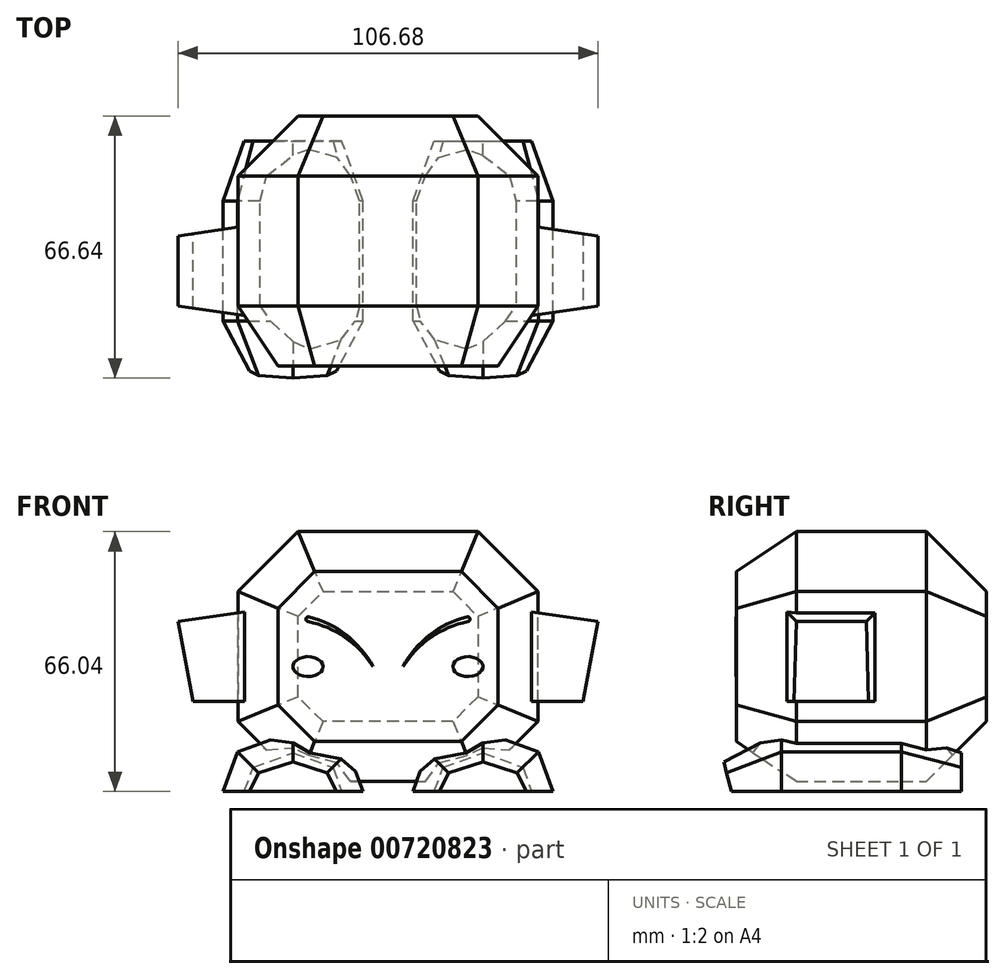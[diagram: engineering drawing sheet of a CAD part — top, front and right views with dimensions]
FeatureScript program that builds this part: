
annotation { "Feature Type Name" : "Feature", "Feature Type Description" : "" }
export const myFeature = defineFeature(function(context is Context, id is Id, definition is map)
    precondition{}
    {
        {
            var Q0;
            Q0=qCreatedBy(makeId("Front.planeOp"),FACE);
            var sketch = newSketch(context, id + "F0", { "sketchPlane" : qUnion([Q0])});
            skLineSegment(sketch, "E0.bottom", {"start": v(38.1, 31.75) * mm, "end": v(-38.1, 31.75) * mm});
            skLineSegment(sketch, "E0.top", {"start": v(38.1, -31.75) * mm, "end": v(-38.1, -31.75) * mm});
            skLineSegment(sketch, "E0.left", {"start": v(38.1, 31.75) * mm, "end": v(38.1, -31.75) * mm});
            skLineSegment(sketch, "E0.right", {"start": v(-38.1, 31.75) * mm, "end": v(-38.1, -31.75) * mm});
            skPoint(sketch, "E0.middle", {"position": v(0, 0) * mm});
            skSolve(sketch);
        }
        {
            var Q0;
            Q0=makeQuery(id+"F0.imprint","IMPRINT",FACE,{"disambiguationData":[TD([[makeQuery(id+"F0.imprint","IMPRINT",EDGE,{"derivedFrom":sQuery(id+"F0.wireOp",EDGE,"E0.bottom")}),1.0]])]});
            extrude(context, id + "F1", {"entities" : qUnion([Q0]), "depth" : 63.5 * mm, "offsetDistance" : 25.4 * mm, "symmetric" : true});
        }
        {
            var Q0;
            Q0=makeQuery(id+"F1.opExtrude","SWEPT_EDGE",EDGE,{"disambiguationData":[OSD([sQuery(id+"F0.wireOp",EDGE,"E0.bottom"),sQuery(id+"F0.wireOp",EDGE,"E0.right")])]});
            var Q1;
            Q1=makeQuery(id+"F1.opExtrude","SWEPT_EDGE",EDGE,{"disambiguationData":[OSD([sQuery(id+"F0.wireOp",EDGE,"E0.bottom"),sQuery(id+"F0.wireOp",EDGE,"E0.left")])]});
            var Q2;
            Q2=makeQuery(id+"F1.opExtrude","SWEPT_EDGE",EDGE,{"disambiguationData":[OSD([sQuery(id+"F0.wireOp",EDGE,"E0.top"),sQuery(id+"F0.wireOp",EDGE,"E0.right")])]});
            var Q3;
            Q3=makeQuery(id+"F1.opExtrude","SWEPT_EDGE",EDGE,{"disambiguationData":[OSD([sQuery(id+"F0.wireOp",EDGE,"E0.top"),sQuery(id+"F0.wireOp",EDGE,"E0.left")])]});
            chamfer(context, id + "F2", {"entities" : qUnion([Q0, Q1, Q2, Q3]), "width" : 15.24 * mm, "tangentPropagation" : true});
        }
        {
            var Q0;
            Q0=makeQuery(id+"F1.opExtrude","CAP_FACE",FACE,{"disambiguationData":[OSD([sQuery(id+"F0.wireOp",EDGE,"E0.bottom"),sQuery(id+"F0.wireOp",EDGE,"E0.top"),sQuery(id+"F0.wireOp",EDGE,"E0.left"),sQuery(id+"F0.wireOp",EDGE,"E0.right")])],"isStart":false});
            chamfer(context, id + "F3", {"entities" : qUnion([Q0]), "chamferType" : ChamferType.TWO_OFFSETS, "width1" : 10.16 * mm, "oppositeDirection" : false, "width2" : 15.24 * mm, "tangentPropagation" : true});
        }
        {
            var Q0;
            Q0=makeQuery(id+"F1.opExtrude","CAP_FACE",FACE,{"disambiguationData":[OSD([sQuery(id+"F0.wireOp",EDGE,"E0.bottom"),sQuery(id+"F0.wireOp",EDGE,"E0.top"),sQuery(id+"F0.wireOp",EDGE,"E0.left"),sQuery(id+"F0.wireOp",EDGE,"E0.right")])],"isStart":true});
            chamfer(context, id + "F4", {"entities" : qUnion([Q0]), "chamferType" : ChamferType.TWO_OFFSETS, "width1" : 15.24 * mm, "oppositeDirection" : false, "width2" : 15.24 * mm, "tangentPropagation" : true});
        }
        {
            var Q0;
            Q0=qCreatedBy(makeId("Right.planeOp"),FACE);
            var sketch = newSketch(context, id + "F5", { "sketchPlane" : qUnion([Q0])});
            skLineSegment(sketch, "E1.bottom", {"start": v(-19.05, 11.43) * mm, "end": v(3.81, 11.43) * mm});
            skLineSegment(sketch, "E1.top", {"start": v(-19.05, -11.43) * mm, "end": v(3.81, -11.43) * mm});
            skLineSegment(sketch, "E1.left", {"start": v(-19.05, 11.43) * mm, "end": v(-19.05, -11.43) * mm});
            skLineSegment(sketch, "E1.right", {"start": v(3.81, 11.43) * mm, "end": v(3.81, -11.43) * mm});
            skPoint(sketch, "E1.middle", {"position": v(-7.62, 0) * mm});
            skSolve(sketch);
        }
        {
            var Q0;
            Q0 = qSketchRegion(id + "F5", true);
            extrude(context, id + "F6", {"entities" : qUnion([Q0]), "operationType" : NewBodyOperationType.ADD, "depth" : 106.68 * mm, "offsetDistance" : 25.4 * mm, "symmetric" : true});
        }
        {
            var Q0;
            Q0=makeQuery(id+"F6.opExtrude","CAP_EDGE",EDGE,{"disambiguationData":[OSD([sQuery(id+"F5.wireOp",EDGE,"E1.bottom")])],"isStart":true});
            var Q1;
            Q1=makeQuery(id+"F6.opExtrude","CAP_EDGE",EDGE,{"disambiguationData":[OSD([sQuery(id+"F5.wireOp",EDGE,"E1.left")])],"isStart":true});
            var Q2;
            Q2=makeQuery(id+"F6.opExtrude","CAP_EDGE",EDGE,{"disambiguationData":[OSD([sQuery(id+"F5.wireOp",EDGE,"E1.right")])],"isStart":true});
            chamfer(context, id + "F7", {"entities" : qUnion([Q0, Q1, Q2]), "chamferType" : ChamferType.TWO_OFFSETS, "width1" : 2.54 * mm, "oppositeDirection" : false, "width2" : 17.78 * mm, "tangentPropagation" : true});
        }
        {
            var Q0;
            Q0=makeQuery(id+"F6.opExtrude","CAP_EDGE",EDGE,{"disambiguationData":[OSD([sQuery(id+"F5.wireOp",EDGE,"E1.left")])],"isStart":false});
            var Q1;
            Q1=makeQuery(id+"F6.opExtrude","CAP_EDGE",EDGE,{"disambiguationData":[OSD([sQuery(id+"F5.wireOp",EDGE,"E1.bottom")])],"isStart":false});
            var Q2;
            Q2=makeQuery(id+"F6.opExtrude","CAP_EDGE",EDGE,{"disambiguationData":[OSD([sQuery(id+"F5.wireOp",EDGE,"E1.right")])],"isStart":false});
            chamfer(context, id + "F8", {"entities" : qUnion([Q0, Q1, Q2]), "chamferType" : ChamferType.TWO_OFFSETS, "width1" : 2.54 * mm, "oppositeDirection" : false, "width2" : 17.78 * mm, "tangentPropagation" : true});
        }
        {
            var Q0;
            Q0=makeQuery(id+"F6.opExtrude","CAP_EDGE",EDGE,{"disambiguationData":[OSD([sQuery(id+"F5.wireOp",EDGE,"E1.top")])],"isStart":true});
            chamfer(context, id + "F9", {"entities" : qUnion([Q0]), "chamferType" : ChamferType.TWO_OFFSETS, "width1" : 3.8 * mm, "oppositeDirection" : false, "width2" : 20.32 * mm, "tangentPropagation" : true});
        }
        {
            var Q0;
            Q0=makeQuery(id+"F6.opExtrude","CAP_EDGE",EDGE,{"disambiguationData":[OSD([sQuery(id+"F5.wireOp",EDGE,"E1.top")])],"isStart":false});
            chamfer(context, id + "F10", {"entities" : qUnion([Q0]), "chamferType" : ChamferType.TWO_OFFSETS, "width1" : 3.8 * mm, "oppositeDirection" : true, "width2" : 20.32 * mm, "tangentPropagation" : true});
        }
        {
            var Q0;
            Q0=makeQuery(id+"F1.opExtrude","CAP_FACE",FACE,{"disambiguationData":[OSD([sQuery(id+"F0.wireOp",EDGE,"E0.bottom"),sQuery(id+"F0.wireOp",EDGE,"E0.top"),sQuery(id+"F0.wireOp",EDGE,"E0.left"),sQuery(id+"F0.wireOp",EDGE,"E0.right")])],"isStart":false});
            var sketch = newSketch(context, id + "F11", { "sketchPlane" : qUnion([Q0])});
            skEllipse(sketch, "E2", {"center": v(-20.32, -2.54) * mm, "majorRadius": 3.81 * mm, "minorRadius": 2.54 * mm, "majorAxis": v(1, 0)});
            skArc(sketch, "E3", {"start": v(-3.81, -2.54) * mm, "mid": v(-10.89, 4.88) * mm, "end": v(-20.32, 8.89) * mm});
            skArc(sketch, "E4", {"start": v(-3.8, -2.54) * mm, "mid": v(-10.58, 5.51) * mm, "end": v(-20.04, 10.13) * mm});
            skCircle(sketch, "E5", {"center": v(-20.2, 9.51) * mm, "radius": 0.64 * mm});
            skCircle(sketch, "E6.MirrorC", {"center": v(20.2, 9.51) * mm, "radius": 0.64 * mm});
            skArc(sketch, "E7.MirrorCS", {"start": v(3.8, -2.54) * mm, "mid": v(10.58, 5.51) * mm, "end": v(20.04, 10.13) * mm});
            skArc(sketch, "E8.MirrorCS", {"start": v(3.81, -2.54) * mm, "mid": v(10.89, 4.88) * mm, "end": v(20.32, 8.89) * mm});
            skEllipse(sketch, "E9.MirrorC", {"center": v(20.32, -2.54) * mm, "majorRadius": 3.81 * mm, "minorRadius": 2.54 * mm, "majorAxis": v(-1, 0)});
            skSolve(sketch);
        }
        {
            var Q0;
            Q0 = qSketchRegion(id + "F11", true);
            extrude(context, id + "F12", {"entities" : qUnion([Q0]), "depth" : 0.03 * mm, "offsetDistance" : 25.4 * mm});
        }
        {
            var Q0;
            Q0=qCreatedBy(makeId("Front.planeOp"),FACE);
            var sketch = newSketch(context, id + "F13", { "sketchPlane" : qUnion([Q0])});
            skLineSegment(sketch, "E10", {"start": v(-6.35, -34.3) * mm, "end": v(-41.91, -34.3) * mm});
            skLineSegment(sketch, "E11", {"start": v(-41.91, -34.3) * mm, "end": v(-38.23, -24.18) * mm});
            skLineSegment(sketch, "E12", {"start": v(-38.23, -24.18) * mm, "end": v(-24.13, -19.05) * mm});
            skPoint(sketch, "E12.endSnap0", {"position": v(-24.13, -34.3) * mm});
            skLineSegment(sketch, "E13", {"start": v(-24.13, -19.05) * mm, "end": v(-24.13, -34.3) * mm});
            skLineSegment(sketch, "E14.MirrorCS", {"start": v(-10.03, -24.18) * mm, "end": v(-24.13, -19.05) * mm});
            skLineSegment(sketch, "E15.MirrorCS", {"start": v(-6.35, -34.3) * mm, "end": v(-10.03, -24.18) * mm});
            skLineSegment(sketch, "E16.MirrorCS", {"start": v(6.35, -34.3) * mm, "end": v(10.03, -24.18) * mm});
            skLineSegment(sketch, "E17.MirrorCS", {"start": v(41.91, -34.3) * mm, "end": v(38.23, -24.18) * mm});
            skLineSegment(sketch, "E18.MirrorCS", {"start": v(6.35, -34.3) * mm, "end": v(41.91, -34.3) * mm});
            skPoint(sketch, "E19.MirrorP", {"position": v(24.13, -34.3) * mm});
            skLineSegment(sketch, "E20.MirrorCS", {"start": v(24.13, -19.05) * mm, "end": v(24.13, -34.3) * mm});
            skLineSegment(sketch, "E21.MirrorCS", {"start": v(10.03, -24.18) * mm, "end": v(24.13, -19.05) * mm});
            skLineSegment(sketch, "E22.MirrorCS", {"start": v(38.23, -24.18) * mm, "end": v(24.13, -19.05) * mm});
            skSolve(sketch);
        }
        {
            var Q0;
            {var subQ0=sQuery(id+"F13.wireOp",EDGE,"E11");Q0=makeQuery(id+"F13.imprint","IMPRINT",FACE,{"disambiguationData":[TD([[makeQuery(id+"F13.imprint","IMPRINT",EDGE,{"derivedFrom":subQ0}),-1.0]])]});}
            var Q1;
            {var subQ2=sQuery(id+"F13.wireOp",EDGE,"E13");Q1=makeQuery(id+"F13.imprint","IMPRINT",FACE,{"disambiguationData":[TD([[makeQuery(id+"F13.imprint","IMPRINT",EDGE,{"derivedFrom":subQ2}),1.0]])]});}
            var Q2;
            {var subQ0=sQuery(id+"F13.wireOp",EDGE,"E16.MirrorCS");Q2=makeQuery(id+"F13.imprint","IMPRINT",FACE,{"disambiguationData":[TD([[makeQuery(id+"F13.imprint","IMPRINT",EDGE,{"derivedFrom":subQ0}),-1.0]])]});}
            var Q3;
            {var subQ0=sQuery(id+"F13.wireOp",EDGE,"E17.MirrorCS");Q3=makeQuery(id+"F13.imprint","IMPRINT",FACE,{"disambiguationData":[TD([[makeQuery(id+"F13.imprint","IMPRINT",EDGE,{"derivedFrom":subQ0}),1.0]])]});}
            extrude(context, id + "F14", {"entities" : qUnion([Q0, Q1, Q2, Q3]), "depth" : 35.56 * mm, "offsetDistance" : 25.4 * mm, "hasSecondDirection" : true, "secondDirectionOppositeDirection" : true, "secondDirectionDepth" : 25.4 * mm});
        }
        {
            var Q0;
            Q0=makeQuery(id+"F14.opExtrude","CAP_EDGE",EDGE,{"disambiguationData":[OSD([sQuery(id+"F13.wireOp",EDGE,"E11")])],"isStart":false});
            var Q1;
            Q1=makeQuery(id+"F14.opExtrude","CAP_EDGE",EDGE,{"disambiguationData":[OSD([sQuery(id+"F13.wireOp",EDGE,"E12")])],"isStart":false});
            var Q2;
            Q2=makeQuery(id+"F14.opExtrude","CAP_EDGE",EDGE,{"disambiguationData":[OSD([sQuery(id+"F13.wireOp",EDGE,"E14.MirrorCS")])],"isStart":false});
            var Q3;
            Q3=makeQuery(id+"F14.opExtrude","CAP_EDGE",EDGE,{"disambiguationData":[OSD([sQuery(id+"F13.wireOp",EDGE,"E15.MirrorCS")])],"isStart":false});
            var Q4;
            Q4=makeQuery(id+"F14.opExtrude","CAP_EDGE",EDGE,{"disambiguationData":[OSD([sQuery(id+"F13.wireOp",EDGE,"E16.MirrorCS")])],"isStart":false});
            var Q5;
            Q5=makeQuery(id+"F14.opExtrude","CAP_EDGE",EDGE,{"disambiguationData":[OSD([sQuery(id+"F13.wireOp",EDGE,"E21.MirrorCS")])],"isStart":false});
            var Q6;
            Q6=makeQuery(id+"F14.opExtrude","CAP_EDGE",EDGE,{"disambiguationData":[OSD([sQuery(id+"F13.wireOp",EDGE,"E22.MirrorCS")])],"isStart":false});
            var Q7;
            Q7=makeQuery(id+"F14.opExtrude","CAP_EDGE",EDGE,{"disambiguationData":[OSD([sQuery(id+"F13.wireOp",EDGE,"E17.MirrorCS")])],"isStart":false});
            chamfer(context, id + "F15", {"entities" : qUnion([Q0, Q1, Q2, Q3, Q4, Q5, Q6, Q7]), "chamferType" : ChamferType.TWO_OFFSETS, "width1" : 15.24 * mm, "oppositeDirection" : false, "width2" : 7.62 * mm, "tangentPropagation" : true});
        }
        {
            var Q0;
            Q0=makeQuery(id+"F14.opExtrude","CAP_EDGE",EDGE,{"disambiguationData":[OSD([sQuery(id+"F13.wireOp",EDGE,"E17.MirrorCS")])],"isStart":true});
            var Q1;
            Q1=makeQuery(id+"F14.opExtrude","CAP_EDGE",EDGE,{"disambiguationData":[OSD([sQuery(id+"F13.wireOp",EDGE,"E22.MirrorCS")])],"isStart":true});
            var Q2;
            Q2=makeQuery(id+"F14.opExtrude","CAP_EDGE",EDGE,{"disambiguationData":[OSD([sQuery(id+"F13.wireOp",EDGE,"E21.MirrorCS")])],"isStart":true});
            var Q3;
            Q3=makeQuery(id+"F14.opExtrude","CAP_EDGE",EDGE,{"disambiguationData":[OSD([sQuery(id+"F13.wireOp",EDGE,"E16.MirrorCS")])],"isStart":true});
            var Q4;
            Q4=makeQuery(id+"F14.opExtrude","CAP_EDGE",EDGE,{"disambiguationData":[OSD([sQuery(id+"F13.wireOp",EDGE,"E15.MirrorCS")])],"isStart":true});
            var Q5;
            Q5=makeQuery(id+"F14.opExtrude","CAP_EDGE",EDGE,{"disambiguationData":[OSD([sQuery(id+"F13.wireOp",EDGE,"E14.MirrorCS")])],"isStart":true});
            var Q6;
            Q6=makeQuery(id+"F14.opExtrude","CAP_EDGE",EDGE,{"disambiguationData":[OSD([sQuery(id+"F13.wireOp",EDGE,"E12")])],"isStart":true});
            var Q7;
            Q7=makeQuery(id+"F14.opExtrude","CAP_EDGE",EDGE,{"disambiguationData":[OSD([sQuery(id+"F13.wireOp",EDGE,"E11")])],"isStart":true});
            chamfer(context, id + "F16", {"entities" : qUnion([Q0, Q1, Q2, Q3, Q4, Q5, Q6, Q7]), "chamferType" : ChamferType.TWO_OFFSETS, "width1" : 15.24 * mm, "oppositeDirection" : false, "width2" : 5.08 * mm, "tangentPropagation" : true});
        }
        {
            var Q0;
            Q0=makeQuery(id+"F14.opExtrude","CAP_EDGE",EDGE,{"disambiguationData":[OSD([sQuery(id+"F13.wireOp",EDGE,"E10")])],"isStart":false});
            chamfer(context, id + "F17", {"entities" : qUnion([Q0]), "chamferType" : ChamferType.TWO_OFFSETS, "width1" : 2.54 * mm, "oppositeDirection" : false, "width2" : 10.16 * mm, "tangentPropagation" : true});
        }
        {
            var Q0;
            Q0=makeQuery(id+"F14.opExtrude","CAP_EDGE",EDGE,{"disambiguationData":[OSD([sQuery(id+"F13.wireOp",EDGE,"E18.MirrorCS")])],"isStart":false});
            chamfer(context, id + "F18", {"entities" : qUnion([Q0]), "chamferType" : ChamferType.TWO_OFFSETS, "width1" : 10.16 * mm, "oppositeDirection" : false, "width2" : 2.54 * mm, "tangentPropagation" : true});
        }
        {
            var Q0;
            Q0=makeQuery(id+"F14.opExtrude","SWEPT_FACE",FACE,{"disambiguationData":[OSD([sQuery(id+"F13.wireOp",EDGE,"E14.MirrorCS")])]});
            var Q1;
            Q1=makeQuery(id+"F14.opExtrude","SWEPT_FACE",FACE,{"disambiguationData":[OSD([sQuery(id+"F13.wireOp",EDGE,"E21.MirrorCS")])]});
            extrude(context, id + "F19", {"entities" : qUnion([Q0, Q1]), "operationType" : NewBodyOperationType.ADD, "depth" : 0.25 * mm, "offsetDistance" : 25.4 * mm});
        }
    });
